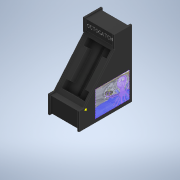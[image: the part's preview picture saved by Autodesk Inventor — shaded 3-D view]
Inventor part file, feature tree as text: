
AUTODESK INVENTOR PART (.ipt)
format: ipt  version: 2020 (Build 240168000, 168)  size: 854,016 bytes
history: native  units: mm
features: sketch x6, extrude x5, other x2, plane x1, mirror x1
ambient origin geometry x8: Origin, YZ Plane, XZ Plane, XY Plane, X Axis, Y Axis, Z Axis, Center Point
bodies: Solid1 (feature_tree)
feature tree (15):
  extrude  "Extrusion1"  Depth=1000.0mm
  extrude  "Extrusion3"  Depth=300.0mm
  extrude  "Extrusion4"  Depth=250.0mm
  extrude  "Extrusion5"  Depth=300.0mm
  extrude  "Extrusion6"  Depth=460.0mm
  plane  "Work Plane1"
  mirror  "Mirror1"
  sketch  "Sketch8"  dims[d11=80.0mm d12=460.0mm]
  sketch  "Sketch9"  dims[d13=40.0mm d14=80.0mm d15=460.0mm d16=40.0mm d17=130.0mm d18=0.0mm d21=110.0mm d22=100.0mm d23=60.0mm d24=60.0mm d25=0.0mm d30=200.0mm d31=300.0mm d32=3.0mm d33=0.0mm d35=30.0mm d36=0.0mm]
  sketch  "Sketch3"  dims[d0=1000.0mm d1=6.981317mm]
  sketch  "Sketch4"  dims[d2=100.0mm d3=300.0mm]
  sketch  "Sketch5"  dims[d4=550.0mm d5=0.0mm d8=250.0mm]
  sketch  "Sketch6"  dims[d9=300.0mm d10=520.0mm]
  other  "Image9"
  other  "Image10"
